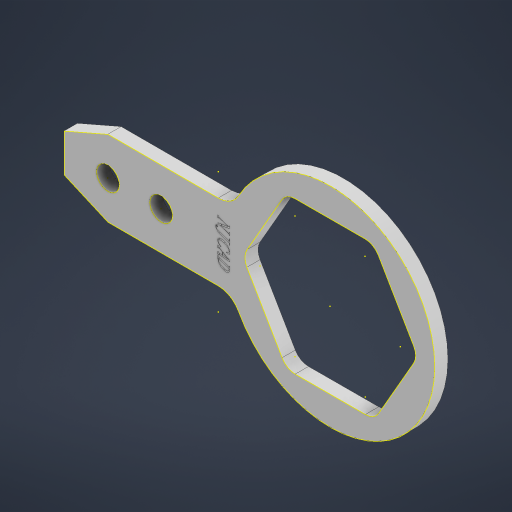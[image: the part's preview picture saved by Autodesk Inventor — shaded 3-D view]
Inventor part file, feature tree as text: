
AUTODESK INVENTOR PART (.ipt)
format: ipt  version: 2023 (Build 270158000, 158)  size: 405,504 bytes
history: native  units: mm
features: sketch x3, extrude x1, emboss x1, projected_geometry x1
ambient origin geometry x8: Origin, YZ Plane, XZ Plane, XY Plane, X Axis, Y Axis, Z Axis, Center Point
bodies: Solid1 (feature_tree)
feature tree (6):
  extrude  "Extrusion1"  Depth=80.0mm
  sketch  "Sketch2"  dims[d3=110.0mm]
  emboss  "Emboss2"
  sketch  "Sketch1"  dims[d1=79.999771mm d2=80.0mm]
  projected_geometry  "Projected Loop1"
  sketch  "Sketch4"  dims[d4=20.0mm d5=140.0mm d6=40.0mm d10=12.0mm d11=8.0mm d12=12.0mm d13=23.0mm d14=28.0mm d15=7.0mm d16=0.0mm d19=1.0mm d20=0.0mm]
